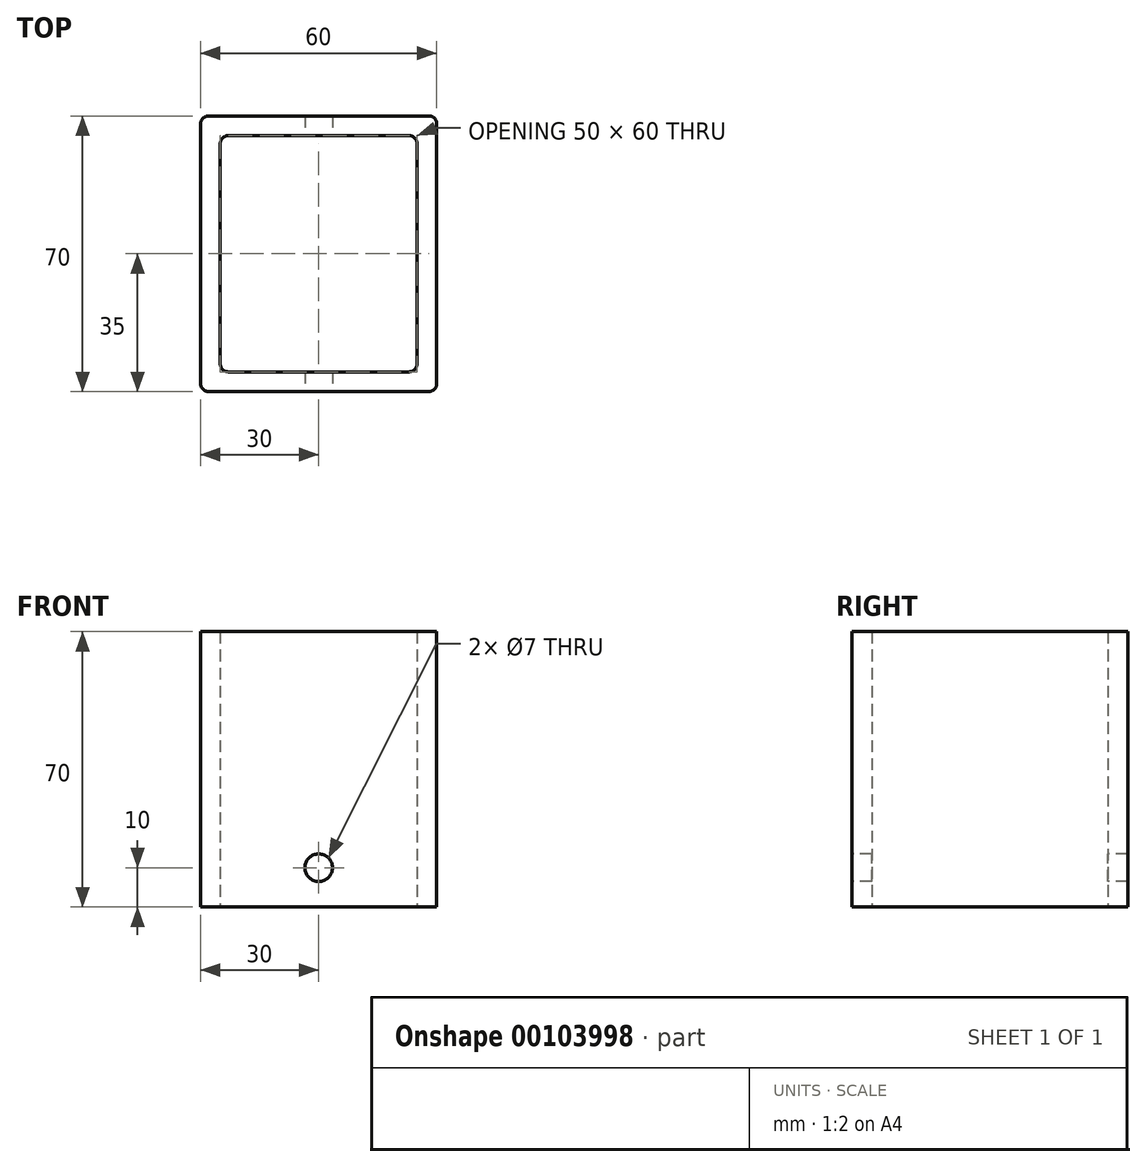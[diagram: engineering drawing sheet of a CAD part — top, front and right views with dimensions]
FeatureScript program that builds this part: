
annotation { "Feature Type Name" : "Feature", "Feature Type Description" : "" }
export const myFeature = defineFeature(function(context is Context, id is Id, definition is map)
    precondition{}
    {
        {
            var Q0;
            Q0=qCreatedBy(makeId("Top.planeOp"),FACE);
            var sketch = newSketch(context, id + "F0", { "sketchPlane" : qUnion([Q0])});
            skLineSegment(sketch, "E0.bottom", {"start": v(30, -35) * mm, "end": v(-30, -35) * mm});
            skLineSegment(sketch, "E0.top", {"start": v(30, 35) * mm, "end": v(-30, 35) * mm});
            skLineSegment(sketch, "E0.left", {"start": v(30, -35) * mm, "end": v(30, 35) * mm});
            skLineSegment(sketch, "E0.right", {"start": v(-30, -35) * mm, "end": v(-30, 35) * mm});
            skPoint(sketch, "E0.middle", {"position": v(0, 0) * mm});
            skLineSegment(sketch, "E1.bottom", {"start": v(25, -30) * mm, "end": v(-25, -30) * mm});
            skLineSegment(sketch, "E1.top", {"start": v(25, 30) * mm, "end": v(-25, 30) * mm});
            skLineSegment(sketch, "E1.left", {"start": v(25, -30) * mm, "end": v(25, 30) * mm});
            skLineSegment(sketch, "E1.right", {"start": v(-25, -30) * mm, "end": v(-25, 30) * mm});
            skSolve(sketch);
        }
        {
            var Q0;
            Q0 = qSketchRegion(id + "F0", true);
            extrude(context, id + "F1", {"entities" : qUnion([Q0]), "depth" : 70 * mm});
        }
        {
            var Q0;
            Q0=makeQuery(id+"F1.opExtrude","SWEPT_EDGE",EDGE,{"disambiguationData":[OSD([sQuery(id+"F0.wireOp",EDGE,"E0.top"),sQuery(id+"F0.wireOp",EDGE,"E0.right")])]});
            var Q1;
            Q1=makeQuery(id+"F1.opExtrude","SWEPT_EDGE",EDGE,{"disambiguationData":[OSD([sQuery(id+"F0.wireOp",EDGE,"E0.top"),sQuery(id+"F0.wireOp",EDGE,"E0.left")])]});
            var Q2;
            Q2=makeQuery(id+"F1.opExtrude","SWEPT_EDGE",EDGE,{"disambiguationData":[OSD([sQuery(id+"F0.wireOp",EDGE,"E0.bottom"),sQuery(id+"F0.wireOp",EDGE,"E0.left")])]});
            var Q3;
            Q3=makeQuery(id+"F1.opExtrude","SWEPT_EDGE",EDGE,{"disambiguationData":[OSD([sQuery(id+"F0.wireOp",EDGE,"E0.bottom"),sQuery(id+"F0.wireOp",EDGE,"E0.right")])]});
            var Q4;
            Q4=makeQuery(id+"F1.opExtrude","SWEPT_EDGE",EDGE,{"disambiguationData":[OSD([sQuery(id+"F0.wireOp",EDGE,"E1.top"),sQuery(id+"F0.wireOp",EDGE,"E1.left")])]});
            var Q5;
            Q5=makeQuery(id+"F1.opExtrude","SWEPT_EDGE",EDGE,{"disambiguationData":[OSD([sQuery(id+"F0.wireOp",EDGE,"E1.bottom"),sQuery(id+"F0.wireOp",EDGE,"E1.right")])]});
            var Q6;
            Q6=makeQuery(id+"F1.opExtrude","SWEPT_EDGE",EDGE,{"disambiguationData":[OSD([sQuery(id+"F0.wireOp",EDGE,"E1.top"),sQuery(id+"F0.wireOp",EDGE,"E1.right")])]});
            var Q7;
            Q7=makeQuery(id+"F1.opExtrude","SWEPT_EDGE",EDGE,{"disambiguationData":[OSD([sQuery(id+"F0.wireOp",EDGE,"E1.bottom"),sQuery(id+"F0.wireOp",EDGE,"E1.left")])]});
            fillet(context, id + "F2", {"entities" : qUnion([Q0, Q1, Q2, Q3, Q4, Q5, Q6, Q7]), "radius" : 2 * mm, "tangentPropagation" : true, "allowEdgeOverflow" : false});
        }
        {
            var Q0;
            Q0=makeQuery(id+"F1.opExtrude","SWEPT_FACE",FACE,{"disambiguationData":[OSD([sQuery(id+"F0.wireOp",EDGE,"E0.bottom")])]});
            var sketch = newSketch(context, id + "F3", { "sketchPlane" : qUnion([Q0])});
            skCircle(sketch, "E2", {"center": v(0, 10) * mm, "radius": 3.5 * mm});
            skSolve(sketch);
        }
        {
            var Q0;
            Q0=makeQuery(id+"F3.imprint","IMPRINT",FACE,{"disambiguationData":[TD([[makeQuery(id+"F3.imprint","IMPRINT",EDGE,{"derivedFrom":sQuery(id+"F3.wireOp",EDGE,"E2")}),1.0]])]});
            extrude(context, id + "F4", {"entities" : qUnion([Q0]), "operationType" : NewBodyOperationType.REMOVE, "oppositeDirection" : true, "depth" : 70 * mm});
        }
    });
